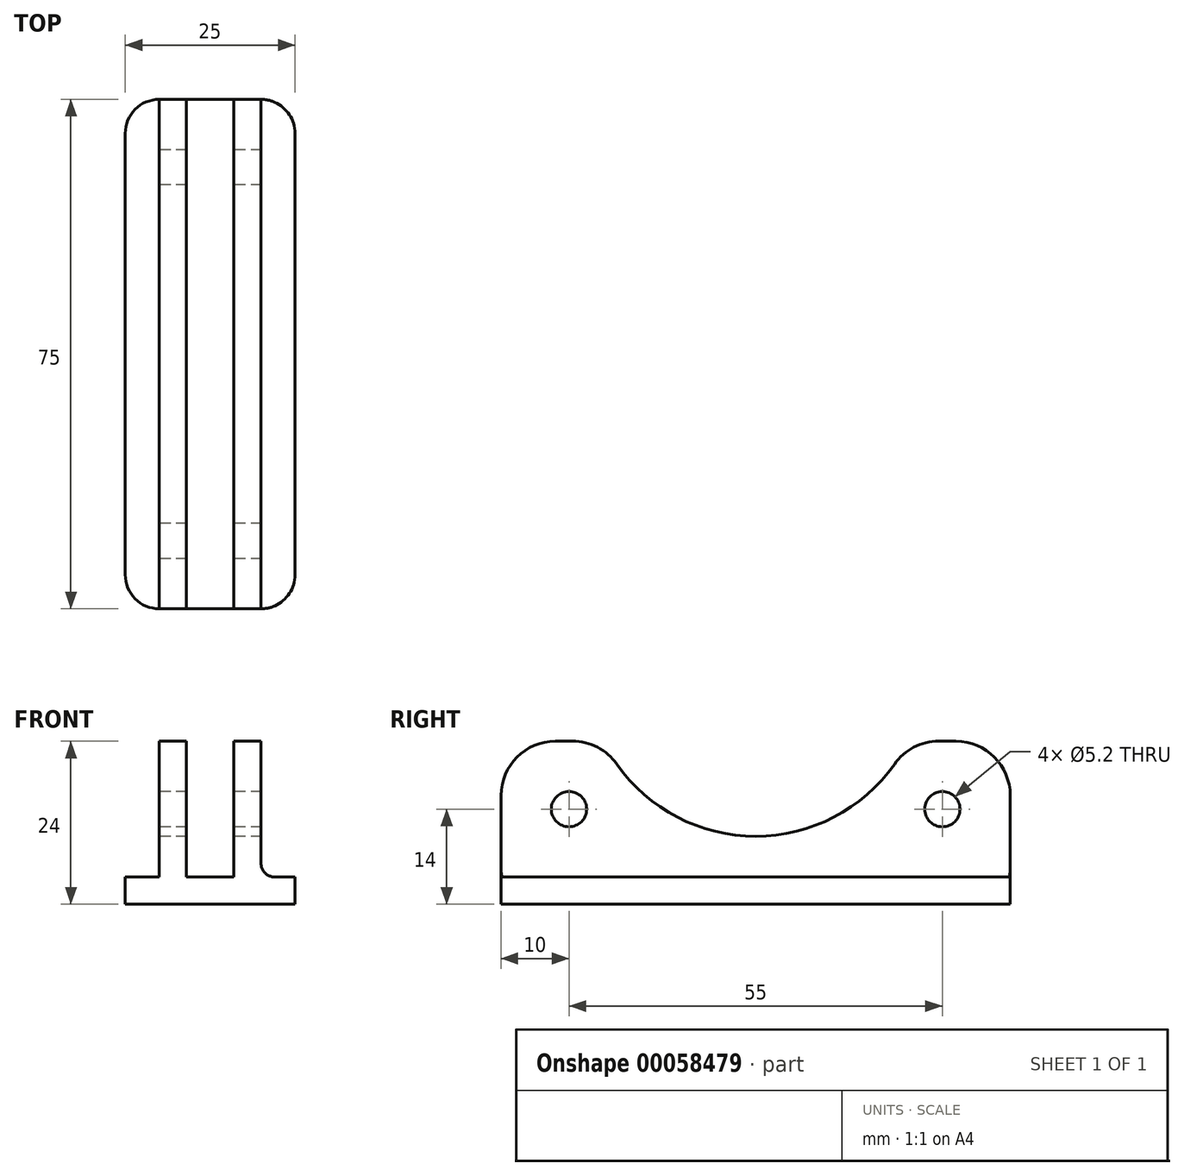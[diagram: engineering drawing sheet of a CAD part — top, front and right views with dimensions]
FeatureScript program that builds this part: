
annotation { "Feature Type Name" : "Feature", "Feature Type Description" : "" }
export const myFeature = defineFeature(function(context is Context, id is Id, definition is map)
    precondition{}
    {
        {
            var Q0;
            Q0=qCreatedBy(makeId("Top.planeOp"),FACE);
            var sketch = newSketch(context, id + "F0", { "sketchPlane" : qUnion([Q0])});
            skLineSegment(sketch, "E0.bottom", {"start": v(-12.5, 37.5) * mm, "end": v(12.5, 37.5) * mm});
            skLineSegment(sketch, "E0.top", {"start": v(-12.5, -37.5) * mm, "end": v(12.5, -37.5) * mm});
            skLineSegment(sketch, "E0.left", {"start": v(-12.5, 37.5) * mm, "end": v(-12.5, -37.5) * mm});
            skLineSegment(sketch, "E0.right", {"start": v(12.5, 37.5) * mm, "end": v(12.5, -37.5) * mm});
            skSolve(sketch);
        }
        {
            var Q0;
            Q0 = qSketchRegion(id + "F0", true);
            extrude(context, id + "F1", {"entities" : qUnion([Q0]), "depth" : 4 * mm});
        }
        {
            var Q0;
            Q0=makeQuery(id+"F1.opExtrude","CAP_FACE",FACE,{"disambiguationData":[OSD([sQuery(id+"F0.wireOp",EDGE,"E0.bottom"),sQuery(id+"F0.wireOp",EDGE,"E0.top"),sQuery(id+"F0.wireOp",EDGE,"E0.left"),sQuery(id+"F0.wireOp",EDGE,"E0.right")])],"isStart":false});
            var sketch = newSketch(context, id + "F2", { "sketchPlane" : qUnion([Q0])});
            skLineSegment(sketch, "E1.bottom", {"start": v(-7.5, 37.5) * mm, "end": v(-3.5, 37.5) * mm});
            skLineSegment(sketch, "E1.top", {"start": v(-7.5, -37.5) * mm, "end": v(-3.5, -37.5) * mm});
            skLineSegment(sketch, "E1.left", {"start": v(-7.5, 37.5) * mm, "end": v(-7.5, -37.5) * mm});
            skLineSegment(sketch, "E1.right", {"start": v(-3.5, 37.5) * mm, "end": v(-3.5, -37.5) * mm});
            skLineSegment(sketch, "E2.bottom", {"start": v(3.5, 37.5) * mm, "end": v(7.5, 37.5) * mm});
            skLineSegment(sketch, "E2.top", {"start": v(3.5, -37.5) * mm, "end": v(7.5, -37.5) * mm});
            skLineSegment(sketch, "E2.left", {"start": v(3.5, 37.5) * mm, "end": v(3.5, -37.5) * mm});
            skLineSegment(sketch, "E2.right", {"start": v(7.5, 37.5) * mm, "end": v(7.5, -37.5) * mm});
            skSolve(sketch);
        }
        {
            var Q0;
            Q0 = qSketchRegion(id + "F2", true);
            extrude(context, id + "F3", {"entities" : qUnion([Q0]), "operationType" : NewBodyOperationType.ADD, "depth" : 20 * mm});
        }
        {
            var Q0;
            Q0=makeQuery(id+"F3.opExtrude","SWEPT_FACE",FACE,{"disambiguationData":[OSD([sQuery(id+"F2.wireOp",EDGE,"E1.left")])]});
            var sketch = newSketch(context, id + "F4", { "sketchPlane" : qUnion([Q0])});
            skCircle(sketch, "E3", {"center": v(0, 35) * mm, "radius": 25 * mm});
            skCircle(sketch, "E4", {"center": v(27.5, 14) * mm, "radius": 2.6 * mm});
            skCircle(sketch, "E5", {"center": v(-27.5, 14) * mm, "radius": 2.6 * mm});
            skLineSegment(sketch, "E6", {"start": v(-37.5, 14) * mm, "end": v(37.5, 14) * mm, "construction": true});
            skSolve(sketch);
        }
        {
            var Q0;
            Q0 = qSketchRegion(id + "F4", true);
            extrude(context, id + "F5", {"entities" : qUnion([Q0]), "operationType" : NewBodyOperationType.REMOVE, "endBound" : BoundingType.THROUGH_ALL, "oppositeDirection" : true, "depth" : 25 * mm});
        }
        {
            var Q0;
            Q0=makeQuery(id+"F5.boolean.opBoolean","INTERSECT",EDGE,{"disambiguationData":[OD(0.0)],"derivedFrom":[makeQuery(id+"F3.opExtrude","CAP_FACE",FACE,{"disambiguationData":[OSD([sQuery(id+"F2.wireOp",EDGE,"E1.bottom"),sQuery(id+"F2.wireOp",EDGE,"E1.top"),sQuery(id+"F2.wireOp",EDGE,"E1.left"),sQuery(id+"F2.wireOp",EDGE,"E1.right")])],"isStart":false}),makeQuery(id+"F5.opExtrude","SWEPT_FACE",FACE,{"disambiguationData":[OSD([sQuery(id+"F4.wireOp",EDGE,"E3")])]})]});
            var Q1;
            Q1=makeQuery(id+"F3.opExtrude","CAP_EDGE",EDGE,{"disambiguationData":[OSD([sQuery(id+"F2.wireOp",EDGE,"E1.bottom")])],"isStart":false});
            var Q2;
            Q2=makeQuery(id+"F3.opExtrude","CAP_EDGE",EDGE,{"disambiguationData":[OSD([sQuery(id+"F2.wireOp",EDGE,"E2.bottom")])],"isStart":false});
            var Q3;
            Q3=makeQuery(id+"F5.boolean.opBoolean","INTERSECT",EDGE,{"disambiguationData":[OD(0.0)],"derivedFrom":[makeQuery(id+"F3.opExtrude","CAP_FACE",FACE,{"disambiguationData":[OSD([sQuery(id+"F2.wireOp",EDGE,"E2.bottom"),sQuery(id+"F2.wireOp",EDGE,"E2.top"),sQuery(id+"F2.wireOp",EDGE,"E2.left"),sQuery(id+"F2.wireOp",EDGE,"E2.right")])],"isStart":false}),makeQuery(id+"F5.opExtrude","SWEPT_FACE",FACE,{"disambiguationData":[OSD([sQuery(id+"F4.wireOp",EDGE,"E3")])]})]});
            var Q4;
            Q4=makeQuery(id+"F5.boolean.opBoolean","INTERSECT",EDGE,{"disambiguationData":[OD(1.0)],"derivedFrom":[makeQuery(id+"F3.opExtrude","CAP_FACE",FACE,{"disambiguationData":[OSD([sQuery(id+"F2.wireOp",EDGE,"E2.bottom"),sQuery(id+"F2.wireOp",EDGE,"E2.top"),sQuery(id+"F2.wireOp",EDGE,"E2.left"),sQuery(id+"F2.wireOp",EDGE,"E2.right")])],"isStart":false}),makeQuery(id+"F5.opExtrude","SWEPT_FACE",FACE,{"disambiguationData":[OSD([sQuery(id+"F4.wireOp",EDGE,"E3")])]})]});
            var Q5;
            Q5=makeQuery(id+"F3.opExtrude","CAP_EDGE",EDGE,{"disambiguationData":[OSD([sQuery(id+"F2.wireOp",EDGE,"E2.top")])],"isStart":false});
            var Q6;
            Q6=makeQuery(id+"F3.opExtrude","CAP_EDGE",EDGE,{"disambiguationData":[OSD([sQuery(id+"F2.wireOp",EDGE,"E1.top")])],"isStart":false});
            var Q7;
            Q7=makeQuery(id+"F5.boolean.opBoolean","INTERSECT",EDGE,{"disambiguationData":[OD(1.0)],"derivedFrom":[makeQuery(id+"F3.opExtrude","CAP_FACE",FACE,{"disambiguationData":[OSD([sQuery(id+"F2.wireOp",EDGE,"E1.bottom"),sQuery(id+"F2.wireOp",EDGE,"E1.top"),sQuery(id+"F2.wireOp",EDGE,"E1.left"),sQuery(id+"F2.wireOp",EDGE,"E1.right")])],"isStart":false}),makeQuery(id+"F5.opExtrude","SWEPT_FACE",FACE,{"disambiguationData":[OSD([sQuery(id+"F4.wireOp",EDGE,"E3")])]})]});
            fillet(context, id + "F6", {"entities" : qUnion([Q0, Q1, Q2, Q3, Q4, Q5, Q6, Q7]), "radius" : 8 * mm, "tangentPropagation" : true, "allowEdgeOverflow" : false});
        }
        {
            var Q0;
            Q0=makeQuery(id+"F1.opExtrude","SWEPT_EDGE",EDGE,{"disambiguationData":[OSD([sQuery(id+"F0.wireOp",EDGE,"E0.top"),sQuery(id+"F0.wireOp",EDGE,"E0.left")])]});
            var Q1;
            Q1=makeQuery(id+"F1.opExtrude","SWEPT_EDGE",EDGE,{"disambiguationData":[OSD([sQuery(id+"F0.wireOp",EDGE,"E0.bottom"),sQuery(id+"F0.wireOp",EDGE,"E0.left")])]});
            var Q2;
            Q2=makeQuery(id+"F1.opExtrude","SWEPT_EDGE",EDGE,{"disambiguationData":[OSD([sQuery(id+"F0.wireOp",EDGE,"E0.bottom"),sQuery(id+"F0.wireOp",EDGE,"E0.right")])]});
            var Q3;
            Q3=makeQuery(id+"F1.opExtrude","SWEPT_EDGE",EDGE,{"disambiguationData":[OSD([sQuery(id+"F0.wireOp",EDGE,"E0.top"),sQuery(id+"F0.wireOp",EDGE,"E0.right")])]});
            fillet(context, id + "F7", {"entities" : qUnion([Q0, Q1, Q2, Q3]), "radius" : 5 * mm, "tangentPropagation" : true, "allowEdgeOverflow" : false});
        }
        {
            var Q0;
            Q0=makeQuery(id+"F3.opExtrude","CAP_EDGE",EDGE,{"disambiguationData":[OSD([sQuery(id+"F2.wireOp",EDGE,"E1.left")])],"isStart":true});
            var Q1;
            Q1=makeQuery(id+"F3.opExtrude","CAP_EDGE",EDGE,{"disambiguationData":[OSD([sQuery(id+"F2.wireOp",EDGE,"E2.right")])],"isStart":true});
            fillet(context, id + "F8", {"entities" : qUnion([Q0, Q1]), "radius" : 2 * mm, "tangentPropagation" : true, "allowEdgeOverflow" : false});
        }
    });
